# Revit family: Plumbing_Drainage_AXOR_42520USA-AXOR-Drain-Finish-set-shower-dr_NEWWW
name_source: partatom
category: Plumbing Fixtures
revit_build: Autodesk Revit 2018 (Build: 20170223_1515(x64)
units: mm (PartAtom-declared; Revit-internal decimal feet)

## family parameters
Cut with Voids When Loaded = Yes
Host = Face
OmniClass Number = 23.31.17.29
OmniClass Title = Shower Drains
Part Type = Normal
Room Calculation Point = No
Round Connector Dimension = Use Diameter
Shared = No

## types (7) — shared parameters
BIMobject category = Drainage
Default Elevation = 1219 mm
Description = AXOR Drain Finish set shower drain 700
Design country = Germany
Edition number = 1
IFC Classification = Sanitary Terminal
Manufacturer = AXOR
Manufacturer country = Germany
Manufacturer name = AXOR
Material 1 = AXOR - Plastic - Dark Gray
Material 2 = AXOR - Plastic - Gray
Model = 42520USA
OmniClass Code = 23-31 17 29
OmniClass Description = Shower Drains
Product Guid = d25766ca-b9ee-49c4-bd8e-6835327a935a
Product SKU = 42520USA
Product data url = https://bimobject.com
Product name = 42520USA AXOR Drain Finish set shower drain 700
Product url = https://www.axor-design.com
QR code = https://bimobject.com
URL = https://www.axor-design.com

## per-type parameters (varying)
| type | Material 3 |
| 001 Chrome | AXOR - Metal - 001 Chrome |
| 251 Brushed Gold Optic | AXOR - Metal - 251 Brushed Gold Optic |
| 341 Brushed Black Chrome | AXOR - Metal - 341 Brushed Black Chrome |
| 671 Matte Black | AXOR - Metal - 671 Matte Black |
| 701 Matte White | AXOR - Metal - 701 Matte White |
| 801 Stainless Steel Optic | AXOR - Metal - 801 Stainless Steel Optic |
| 821 Brushed Nickel | AXOR - Metal - 821 Brushed Nickel |

## geometry (parser evidence)
native form markers: Sweep x6
no freeform markers — native parametric forms only
